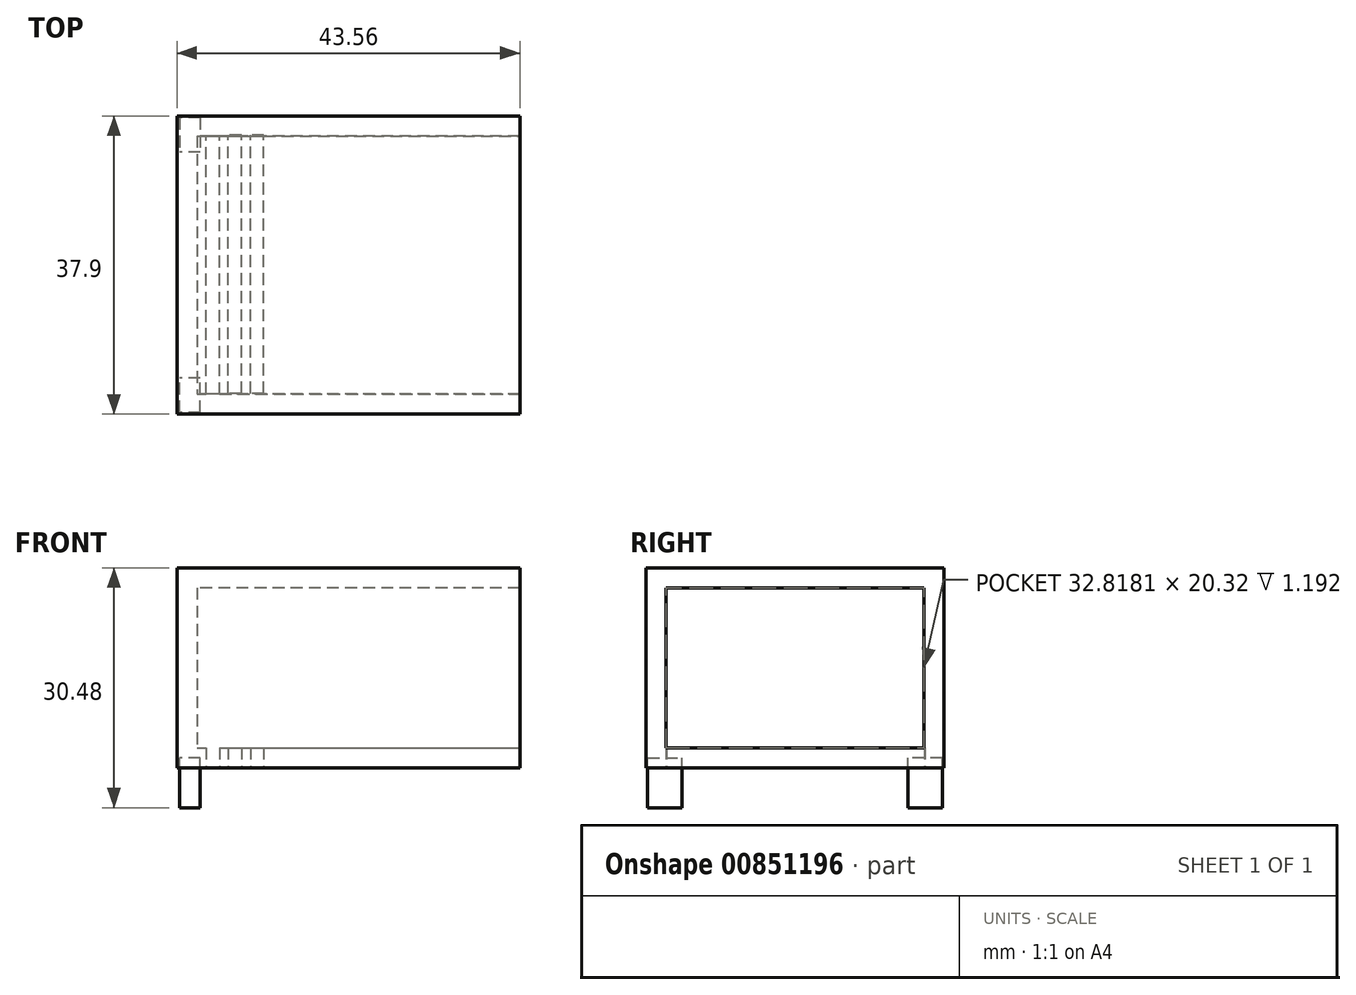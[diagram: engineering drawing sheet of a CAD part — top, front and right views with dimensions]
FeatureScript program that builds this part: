
annotation { "Feature Type Name" : "Feature", "Feature Type Description" : "" }
export const myFeature = defineFeature(function(context is Context, id is Id, definition is map)
    precondition{}
    {
        {
            var Q0;
            Q0=qCreatedBy(makeId("Top.planeOp"),FACE);
            var sketch = newSketch(context, id + "F0", { "sketchPlane" : qUnion([Q0])});
            skLineSegment(sketch, "E0.bottom", {"start": v(0, 18.95) * mm, "end": v(-43.56, 18.95) * mm});
            skLineSegment(sketch, "E0.top", {"start": v(0, -18.95) * mm, "end": v(-43.56, -18.95) * mm});
            skLineSegment(sketch, "E0.left", {"start": v(0, 18.95) * mm, "end": v(0, -18.95) * mm});
            skLineSegment(sketch, "E0.right", {"start": v(-43.56, 18.95) * mm, "end": v(-43.56, -18.95) * mm});
            skSolve(sketch);
        }
        {
            var Q0;
            Q0 = qSketchRegion(id + "F0", true);
            extrude(context, id + "F1", {"entities" : qUnion([Q0]), "depth" : 25.4 * mm, "offsetDistance" : 25.4 * mm});
        }
        {
            var Q0;
            Q0=makeQuery(id+"F1.opExtrude","SWEPT_FACE",FACE,{"disambiguationData":[OSD([sQuery(id+"F0.wireOp",EDGE,"E0.left")])]});
            shell(context, id + "F2", {"entities" : qUnion([Q0]), "thickness" : 2.54 * mm});
        }
        {
            var Q0;
            Q0=makeQuery(id+"F1.opExtrude","CAP_FACE",FACE,{"disambiguationData":[OSD([sQuery(id+"F0.wireOp",EDGE,"E0.bottom"),sQuery(id+"F0.wireOp",EDGE,"E0.top"),sQuery(id+"F0.wireOp",EDGE,"E0.left"),sQuery(id+"F0.wireOp",EDGE,"E0.right")])],"isStart":true});
            var sketch = newSketch(context, id + "F3", { "sketchPlane" : qUnion([Q0])});
            skLineSegment(sketch, "E1.bottom", {"start": v(-38.14, 16.41) * mm, "end": v(-39.83, 16.41) * mm});
            skLineSegment(sketch, "E1.top", {"start": v(-38.14, -16.41) * mm, "end": v(-39.83, -16.41) * mm});
            skLineSegment(sketch, "E1.left", {"start": v(-38.14, 16.41) * mm, "end": v(-38.14, -16.41) * mm});
            skLineSegment(sketch, "E1.right", {"start": v(-39.83, 16.41) * mm, "end": v(-39.83, -16.41) * mm});
            skPoint(sketch, "E1.middle", {"position": v(-38.99, 0) * mm});
            skLineSegment(sketch, "E2.bottom", {"start": v(-35.37, 16.32) * mm, "end": v(-37.06, 16.32) * mm});
            skLineSegment(sketch, "E2.top", {"start": v(-35.37, -16.5) * mm, "end": v(-37.06, -16.5) * mm});
            skLineSegment(sketch, "E2.left", {"start": v(-35.37, 16.32) * mm, "end": v(-35.37, -16.5) * mm});
            skLineSegment(sketch, "E2.right", {"start": v(-37.06, 16.32) * mm, "end": v(-37.06, -16.5) * mm});
            skPoint(sketch, "E2.middle", {"position": v(-36.22, -0.09) * mm});
            skLineSegment(sketch, "E3.bottom", {"start": v(-32.54, 16.32) * mm, "end": v(-34.23, 16.32) * mm});
            skLineSegment(sketch, "E3.top", {"start": v(-32.54, -16.5) * mm, "end": v(-34.23, -16.5) * mm});
            skLineSegment(sketch, "E3.left", {"start": v(-32.54, 16.32) * mm, "end": v(-32.54, -16.5) * mm});
            skLineSegment(sketch, "E3.right", {"start": v(-34.23, 16.32) * mm, "end": v(-34.23, -16.5) * mm});
            skPoint(sketch, "E3.middle", {"position": v(-33.39, -0.09) * mm});
            skSolve(sketch);
        }
        {
            var Q0;
            Q0 = qSketchRegion(id + "F3", true);
            extrude(context, id + "F4", {"entities" : qUnion([Q0]), "operationType" : NewBodyOperationType.REMOVE, "oppositeDirection" : true, "depth" : 2.54 * mm, "offsetDistance" : 25.4 * mm});
        }
        {
            var Q0;
            Q0=makeQuery(id+"F1.opExtrude","CAP_FACE",FACE,{"disambiguationData":[OSD([sQuery(id+"F0.wireOp",EDGE,"E0.bottom"),sQuery(id+"F0.wireOp",EDGE,"E0.top"),sQuery(id+"F0.wireOp",EDGE,"E0.left"),sQuery(id+"F0.wireOp",EDGE,"E0.right")])],"isStart":true});
            var sketch = newSketch(context, id + "F5", { "sketchPlane" : qUnion([Q0])});
            skLineSegment(sketch, "E4.bottom", {"start": v(-40.6, 18.73) * mm, "end": v(-43.24, 18.73) * mm});
            skLineSegment(sketch, "E4.top", {"start": v(-40.6, 14.38) * mm, "end": v(-43.24, 14.38) * mm});
            skLineSegment(sketch, "E4.left", {"start": v(-40.6, 18.73) * mm, "end": v(-40.6, 14.38) * mm});
            skLineSegment(sketch, "E4.right", {"start": v(-43.24, 18.73) * mm, "end": v(-43.24, 14.38) * mm});
            skPoint(sketch, "E4.middle", {"position": v(-41.92, 16.55) * mm});
            skLineSegment(sketch, "E5", {"start": v(-56, 0) * mm, "end": v(0, 0) * mm, "construction": true});
            skLineSegment(sketch, "E6.MirrorCS", {"start": v(-40.6, -14.38) * mm, "end": v(-43.24, -14.38) * mm});
            skLineSegment(sketch, "E7.MirrorCS", {"start": v(-40.6, -18.73) * mm, "end": v(-40.6, -14.38) * mm});
            skLineSegment(sketch, "E8.MirrorCS", {"start": v(-43.24, -18.73) * mm, "end": v(-43.24, -14.38) * mm});
            skLineSegment(sketch, "E9.MirrorCS", {"start": v(-40.6, -18.73) * mm, "end": v(-43.24, -18.73) * mm});
            skPoint(sketch, "E10.MirrorP", {"position": v(-41.92, -16.55) * mm});
            skSolve(sketch);
        }
        {
            var Q0;
            Q0 = qSketchRegion(id + "F5", true);
            extrude(context, id + "F6", {"entities" : qUnion([Q0]), "depth" : 5.08 * mm, "offsetDistance" : 25.4 * mm, "hasSecondDirection" : true, "secondDirectionOppositeDirection" : true, "secondDirectionDepth" : 1.27 * mm});
        }
    });
